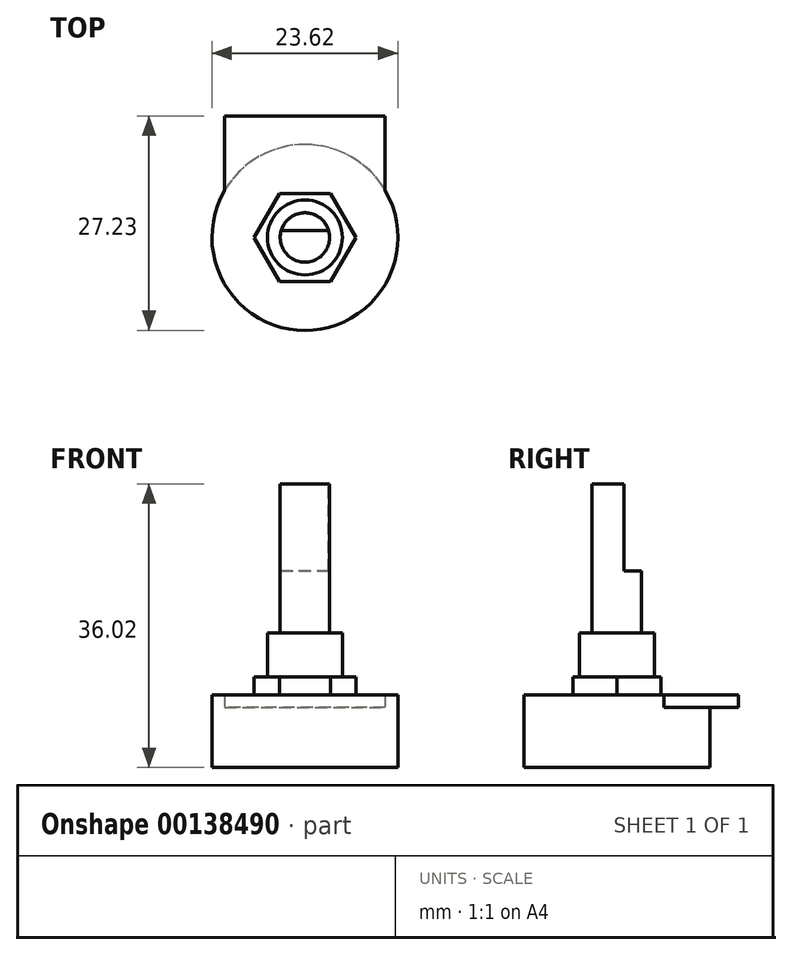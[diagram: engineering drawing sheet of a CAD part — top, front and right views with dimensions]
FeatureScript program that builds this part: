
annotation { "Feature Type Name" : "Feature", "Feature Type Description" : "" }
export const myFeature = defineFeature(function(context is Context, id is Id, definition is map)
    precondition{}
    {
        {
            var Q0;
            Q0=qCreatedBy(makeId("Top.planeOp"),FACE);
            var sketch = newSketch(context, id + "F0", { "sketchPlane" : qUnion([Q0])});
            skCircle(sketch, "E0", {"center": v(0, 0) * mm, "radius": 11.81 * mm});
            skSolve(sketch);
        }
        {
            var Q0;
            Q0=qSketchRegion(id+"F0",true);
            extrude(context, id + "F1", {"entities" : qUnion([Q0]), "depth" : 7.65 * mm});
        }
        {
            var Q0;
            Q0=makeQuery(id+"F1.opExtrude","CAP_FACE",FACE,{"disambiguationData":[OSD([sQuery(id+"F0.wireOp",EDGE,"E0")])],"isStart":false});
            var sketch = newSketch(context, id + "F2", { "sketchPlane" : qUnion([Q0])});
            skLineSegment(sketch, "E1", {"start": v(0, 0) * mm, "end": v(0, 15.42) * mm, "construction": true});
            skLineSegment(sketch, "E2.bottom", {"start": v(-10.2, 15.42) * mm, "end": v(10.2, 15.42) * mm});
            skLineSegment(sketch, "E2.left", {"start": v(-10.2, 15.42) * mm, "end": v(-10.2, 5.96) * mm});
            skLineSegment(sketch, "E2.right", {"start": v(10.2, 15.42) * mm, "end": v(10.2, 5.96) * mm});
            skArc(sketch, "E3", {"start": v(-10.2, 5.96) * mm, "mid": v(0, -11.81) * mm, "end": v(10.2, 5.96) * mm});
            skSolve(sketch);
        }
        {
            var Q0;
            Q0=qSketchRegion(id+"F2",true);
            extrude(context, id + "F3", {"entities" : qUnion([Q0]), "operationType" : NewBodyOperationType.ADD, "depth" : 1.57 * mm});
        }
        {
            var Q0;
            Q0=makeQuery(id+"F3.opExtrude","CAP_FACE",FACE,{"disambiguationData":[OSD([sQuery(id+"F2.wireOp",EDGE,"E2.bottom"),sQuery(id+"F2.wireOp",EDGE,"E2.left"),sQuery(id+"F2.wireOp",EDGE,"E2.right"),sQuery(id+"F2.wireOp",EDGE,"E3")])],"isStart":false});
            var sketch = newSketch(context, id + "F4", { "sketchPlane" : qUnion([Q0])});
            skCircle(sketch, "E4.cCircle", {"center": v(0, 0) * mm, "radius": 5.6 * mm, "construction": true});
            skLineSegment(sketch, "E4.0", {"start": v(3.23, -5.6) * mm, "end": v(-3.23, -5.6) * mm});
            skLineSegment(sketch, "E4.1", {"start": v(-3.23, -5.6) * mm, "end": v(-6.47, 0) * mm});
            skLineSegment(sketch, "E4.2", {"start": v(-6.47, 0) * mm, "end": v(-3.23, 5.6) * mm});
            skLineSegment(sketch, "E4.3", {"start": v(-3.23, 5.6) * mm, "end": v(3.23, 5.6) * mm});
            skLineSegment(sketch, "E4.4", {"start": v(3.23, 5.6) * mm, "end": v(6.47, 0) * mm});
            skLineSegment(sketch, "E4.5", {"start": v(6.47, 0) * mm, "end": v(3.23, -5.6) * mm});
            skPoint(sketch, "E4.0.midPoint", {"position": v(0, -5.6) * mm});
            skSolve(sketch);
        }
        {
            var Q0;
            Q0=qSketchRegion(id+"F4",true);
            extrude(context, id + "F5", {"entities" : qUnion([Q0]), "operationType" : NewBodyOperationType.ADD, "depth" : 2.3 * mm});
        }
        {
            var Q0;
            Q0=makeQuery(id+"F5.opExtrude","CAP_FACE",FACE,{"disambiguationData":[OSD([sQuery(id+"F4.wireOp",EDGE,"E4.0"),sQuery(id+"F4.wireOp",EDGE,"E4.1"),sQuery(id+"F4.wireOp",EDGE,"E4.2"),sQuery(id+"F4.wireOp",EDGE,"E4.3"),sQuery(id+"F4.wireOp",EDGE,"E4.4"),sQuery(id+"F4.wireOp",EDGE,"E4.5")])],"isStart":false});
            var sketch = newSketch(context, id + "F6", { "sketchPlane" : qUnion([Q0])});
            skCircle(sketch, "E5", {"center": v(0, 0) * mm, "radius": 4.76 * mm});
            skSolve(sketch);
        }
        {
            var Q0;
            Q0=qSketchRegion(id+"F6",true);
            extrude(context, id + "F7", {"entities" : qUnion([Q0]), "operationType" : NewBodyOperationType.ADD, "depth" : 5.6 * mm});
        }
        {
            var Q0;
            Q0=makeQuery(id+"F7.opExtrude","CAP_FACE",FACE,{"disambiguationData":[OSD([sQuery(id+"F6.wireOp",EDGE,"E5")])],"isStart":false});
            var sketch = newSketch(context, id + "F8", { "sketchPlane" : qUnion([Q0])});
            skCircle(sketch, "E6", {"center": v(0, 0) * mm, "radius": 3.14 * mm});
            skSolve(sketch);
        }
        {
            var Q0;
            Q0=qSketchRegion(id+"F8",true);
            extrude(context, id + "F9", {"entities" : qUnion([Q0]), "operationType" : NewBodyOperationType.ADD, "depth" : 18.92 * mm});
        }
        {
            var Q0;
            Q0=makeQuery(id+"F9.opExtrude","CAP_FACE",FACE,{"disambiguationData":[OSD([sQuery(id+"F8.wireOp",EDGE,"E6")])],"isStart":false});
            var sketch = newSketch(context, id + "F10", { "sketchPlane" : qUnion([Q0])});
            skLineSegment(sketch, "E7", {"start": v(0, 0) * mm, "end": v(0, 0.88) * mm, "construction": true});
            skLineSegment(sketch, "E8.bottom", {"start": v(-3.01, 0.88) * mm, "end": v(3.01, 0.88) * mm});
            skLineSegment(sketch, "E8.top", {"start": v(-3.01, 3.14) * mm, "end": v(3.01, 3.14) * mm});
            skLineSegment(sketch, "E8.left", {"start": v(-3.01, 0.88) * mm, "end": v(-3.01, 3.14) * mm});
            skLineSegment(sketch, "E8.right", {"start": v(3.01, 0.88) * mm, "end": v(3.01, 3.14) * mm});
            skSolve(sketch);
        }
        {
            var Q0;
            Q0=qSketchRegion(id+"F10",true);
            extrude(context, id + "F11", {"entities" : qUnion([Q0]), "operationType" : NewBodyOperationType.REMOVE, "oppositeDirection" : true, "depth" : 11.05 * mm});
        }
    });
